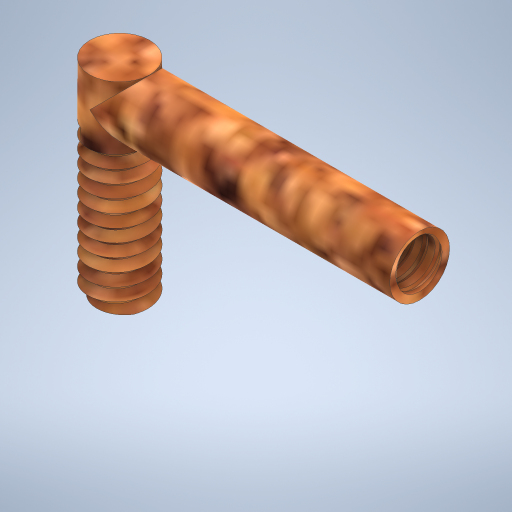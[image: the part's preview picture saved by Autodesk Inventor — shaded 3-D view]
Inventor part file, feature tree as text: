
AUTODESK INVENTOR PART (.ipt)
format: ipt  version: 2024 (Build 280153020, 153B)  size: 883,712 bytes
history: native  units: mm
features: sketch x5, extrude x3, helix x2, plane x1
ambient origin geometry x8: Origin, YZ Plane, XZ Plane, XY Plane, X Axis, Y Axis, Z Axis, Center Point
bodies: Solid1 (feature_tree)
feature tree (11):
  extrude  "Extrusion1"  Depth=1.7mm TaperAngle=0.0deg
  helix  "Coil1"  [1 undecoded]
  extrude  "Extrusion2"  Depth=0.2mm
  extrude  "Extrusion3"  Depth=1.7mm
  plane  "Work Plane1"
  helix  "Coil2"  [1 undecoded]
  sketch  "Sketch1"  dims[d0=8.0mm d1=27.0mm d2=0.0mm d3=1.7mm]
  sketch  "Sketch2"  dims[d4=60.0deg d5=0.2mm]
  sketch  "Sketch4"  dims[d6=2.0mm]
  sketch  "Sketch5"  dims[d7=1.7mm d8=22.0mm d9=10.0mm d10=0.0mm d11=90.0deg d12=90.0deg d13=0.0mm d14=0.0mm d15=8.0mm d16=40.0mm d17=0.0mm]
  sketch  "Sketch7"  dims[d18=6.0mm d19=25.0mm d20=0.0mm d28=23.0mm d29=1.7mm d30=60.0deg d31=2.2mm d32=2.0mm d33=0.2mm d34=1.7mm d35=27.0mm d36=10.0mm d37=0.0mm d38=90.0deg d39=90.0deg d40=0.0mm d41=0.0mm]
note: 2 required parameter values undecoded (feature->parameter linkage not recoverable at this tier; creation-order binding heuristic only, values carry confidence <= 0.55)
